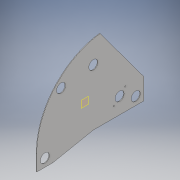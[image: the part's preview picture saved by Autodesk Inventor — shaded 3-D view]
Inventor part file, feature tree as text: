
AUTODESK INVENTOR PART (.ipt)
format: ipt  version: 2018 (Build 220112000, 112)  size: 179,712 bytes
history: native  units: in
note: dims shown in document units (in); Inventor stores cm internally (conversion verified against a paired STEP export)
features: extrude x5, sketch x4, plane x2, projected_geometry x1
ambient origin geometry x8: Origin, YZ Plane, XZ Plane, XY Plane, X Axis, Y Axis, Z Axis, Center Point
bodies: Body1 (feature_tree)
feature tree (12):
  sketch  "Sketch1"  dims[d2=1.1225in d5=11.0in]
  plane  "Work Plane2"
  sketch  "Sketch2"  dims[d8=1.0in d9=1.0in]
  plane  "Work Plane1"
  extrude  "Extrusion6"  Depth=11.0in
  extrude  "Extrusion7"  Depth=1.0in
  extrude  "Extrusion8"  Depth=6.0in
  extrude  "Extrusion9"  Depth=0.07in
  extrude  "Extrusion10"  Depth=0.07in
  sketch  "Sketch4"  dims[d11=6.0in d12=6.0in]
  projected_geometry  "Projected Loop1"
  sketch  "Sketch5"  dims[d13=1.125in d14=5.5in d15=2.0in d16=1.125in d22=10.0in d24=1.0in d25=1.125in d28=2.0in d29=1.0in d30=2.0in d31=1.125in d34=9.0in d35=1.5in d36=12.25in d37=0.707in d38=0.707in d39=0.707in d40=0.707in d45=0.159in d46=0.159in d47=1.0in d48=2.0in d49=1.0in d50=1.125in d51=0.07in d52=0.0in d53=0.07in d54=0.0in d55=0.07in d56=0.0in d57=0.07in d58=0.0in d59=0.07in d60=0.0in]
